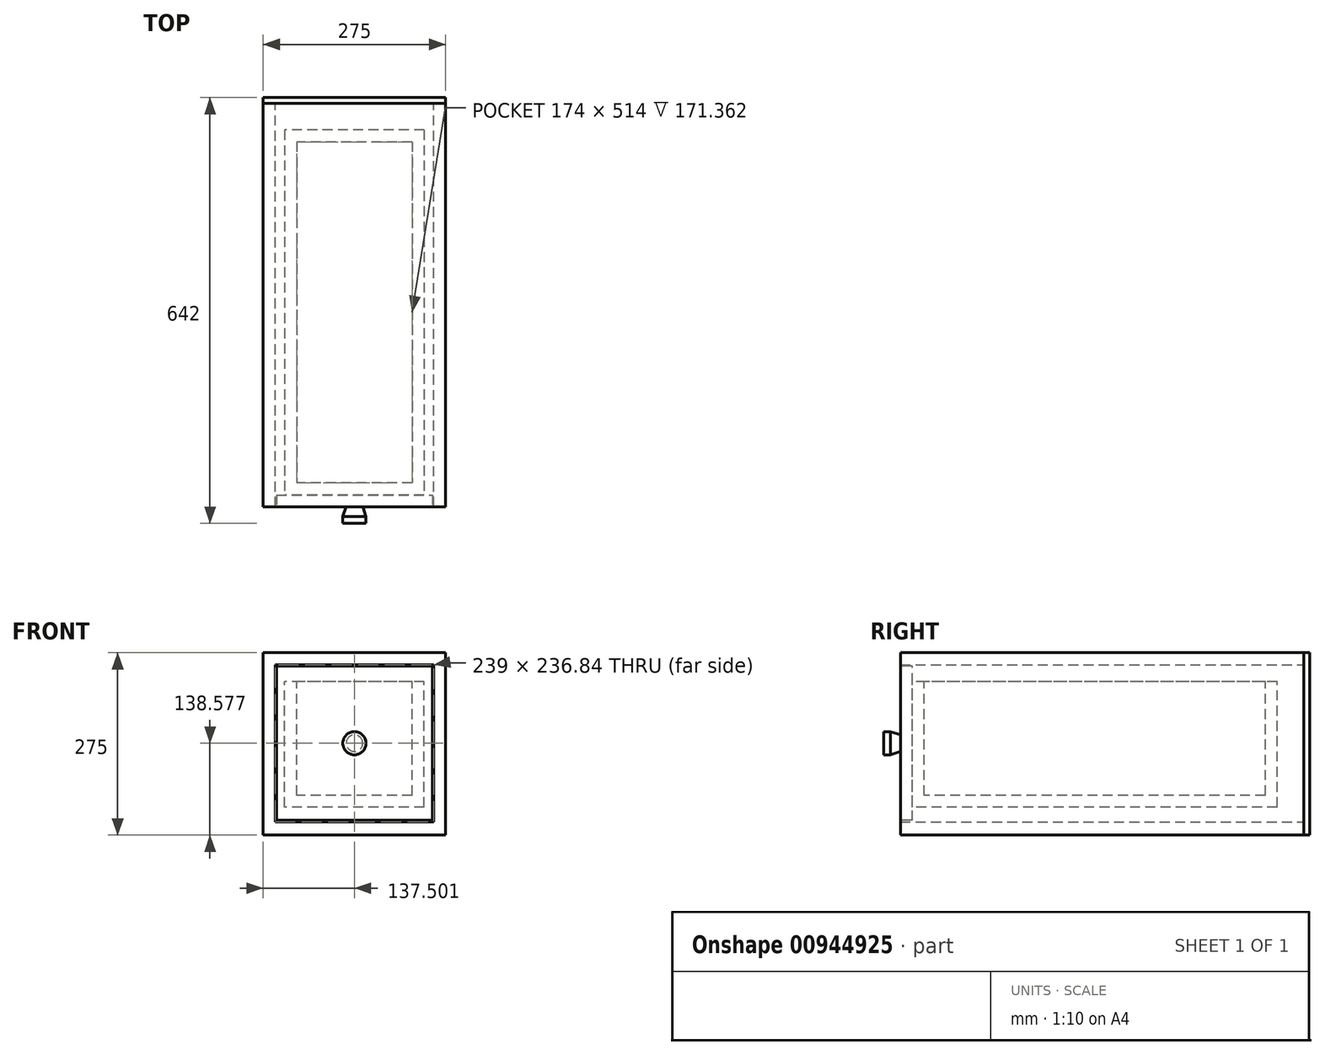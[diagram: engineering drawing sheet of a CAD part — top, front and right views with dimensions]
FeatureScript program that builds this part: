
annotation { "Feature Type Name" : "Feature", "Feature Type Description" : "" }
export const myFeature = defineFeature(function(context is Context, id is Id, definition is map)
    precondition{}
    {
        {
            var Q0;
            Q0=qCreatedBy(makeId("Front.planeOp"),FACE);
            var sketch = newSketch(context, id + "F0", { "sketchPlane" : qUnion([Q0])});
            skLineSegment(sketch, "E0", {"start": v(-326.85, -71.54) * mm, "end": v(-326.85, 203.46) * mm});
            skLineSegment(sketch, "E1.1", {"start": v(-308.85, -51.38) * mm, "end": v(-308.85, 185.46) * mm});
            skLineSegment(sketch, "E2.trimOffspring", {"start": v(-69.85, -51.38) * mm, "end": v(-308.85, -51.38) * mm});
            skLineSegment(sketch, "E3.top", {"start": v(-308.85, 185.46) * mm, "end": v(-69.85, 185.46) * mm});
            skLineSegment(sketch, "E4.trimOffspring", {"start": v(-69.85, 185.46) * mm, "end": v(-69.85, -51.38) * mm});
            skLineSegment(sketch, "E5", {"start": v(-326.85, 203.46) * mm, "end": v(-51.85, 203.46) * mm});
            skLineSegment(sketch, "E6", {"start": v(-51.85, -71.54) * mm, "end": v(-51.85, 203.46) * mm});
            skLineSegment(sketch, "E7", {"start": v(-326.85, -71.54) * mm, "end": v(-51.85, -71.54) * mm});
            skSolve(sketch);
        }
        {
            var Q0;
            Q0=qSketchRegion(id+"F0",true);
            extrude(context, id + "F1", {"entities" : qUnion([Q0]), "depth" : 608 * mm, "offsetDistance" : 25 * mm});
        }
        {
            var Q0;
            Q0=makeQuery(id+"F1.opExtrude","CAP_FACE",FACE,{"disambiguationData":[OSD([sQuery(id+"F0.wireOp",EDGE,"E0"),sQuery(id+"F0.wireOp",EDGE,"1bbb11d5-5f90-4ef2-9ceb-a32cb31813a0"),sQuery(id+"F0.wireOp",EDGE,"E1.1"),sQuery(id+"F0.wireOp",EDGE,"E2.trimOffspring"),sQuery(id+"F0.wireOp",EDGE,"E3.top"),sQuery(id+"F0.wireOp",EDGE,"E4.trimOffspring"),sQuery(id+"F0.wireOp",EDGE,"E5"),sQuery(id+"F0.wireOp",EDGE,"E6")])],"isStart":true});
            var sketch = newSketch(context, id + "F2", { "sketchPlane" : qUnion([Q0])});
            skLineSegment(sketch, "E8.left", {"start": v(51.85, 203.46) * mm, "end": v(51.85, 203.46) * mm});
            skLineSegment(sketch, "E8.right", {"start": v(326.85, 203.46) * mm, "end": v(326.85, 203.46) * mm});
            skLineSegment(sketch, "E9.bottom", {"start": v(51.85, 203.46) * mm, "end": v(326.85, 203.46) * mm});
            skLineSegment(sketch, "E9.top", {"start": v(51.85, -71.54) * mm, "end": v(326.85, -71.54) * mm});
            skLineSegment(sketch, "E9.left", {"start": v(51.85, 203.46) * mm, "end": v(51.85, -71.54) * mm});
            skLineSegment(sketch, "E9.right", {"start": v(326.85, 203.46) * mm, "end": v(326.85, -71.54) * mm});
            skSolve(sketch);
        }
        {
            var Q0;
            Q0=qSketchRegion(id+"F2",true);
            extrude(context, id + "F3", {"entities" : qUnion([Q0]), "depth" : 9 * mm, "offsetDistance" : 25 * mm});
        }
        {
            var Q0;
            Q0=makeQuery(id+"F1.opExtrude","CAP_FACE",FACE,{"disambiguationData":[OSD([sQuery(id+"F0.wireOp",EDGE,"E0"),sQuery(id+"F0.wireOp",EDGE,"1bbb11d5-5f90-4ef2-9ceb-a32cb31813a0"),sQuery(id+"F0.wireOp",EDGE,"E1.1"),sQuery(id+"F0.wireOp",EDGE,"E2.trimOffspring"),sQuery(id+"F0.wireOp",EDGE,"E3.top"),sQuery(id+"F0.wireOp",EDGE,"E4.trimOffspring"),sQuery(id+"F0.wireOp",EDGE,"E5"),sQuery(id+"F0.wireOp",EDGE,"E6")])],"isStart":false});
            var sketch = newSketch(context, id + "F4", { "sketchPlane" : qUnion([Q0])});
            skLineSegment(sketch, "E10.0", {"start": v(-306.85, 183.46) * mm, "end": v(-71.85, 183.46) * mm});
            skLineSegment(sketch, "E10.1", {"start": v(-306.85, -49.38) * mm, "end": v(-306.85, 183.46) * mm});
            skLineSegment(sketch, "E10.2", {"start": v(-71.85, -49.38) * mm, "end": v(-306.85, -49.38) * mm});
            skLineSegment(sketch, "E10.3", {"start": v(-71.85, 183.46) * mm, "end": v(-71.85, -49.38) * mm});
            skSolve(sketch);
        }
        {
            var Q0;
            Q0=qSketchRegion(id+"F4",true);
            extrude(context, id + "F5", {"entities" : qUnion([Q0]), "oppositeDirection" : true, "depth" : 18 * mm, "offsetDistance" : 25 * mm});
        }
        {
            var Q0;
            Q0=makeQuery(id+"F5.opExtrude","CAP_FACE",FACE,{"disambiguationData":[OSD([sQuery(id+"F4.wireOp",EDGE,"E10.0"),sQuery(id+"F4.wireOp",EDGE,"E10.1"),sQuery(id+"F4.wireOp",EDGE,"E10.2"),sQuery(id+"F4.wireOp",EDGE,"E10.3")])],"isStart":false});
            var sketch = newSketch(context, id + "F6", { "sketchPlane" : qUnion([Q0])});
            skLineSegment(sketch, "E11.bottom", {"start": v(84.35, -29.38) * mm, "end": v(294.35, -29.38) * mm});
            skLineSegment(sketch, "E11.top", {"start": v(84.35, 159.98) * mm, "end": v(294.35, 159.98) * mm});
            skLineSegment(sketch, "E11.left", {"start": v(84.35, -29.38) * mm, "end": v(84.35, 159.98) * mm});
            skLineSegment(sketch, "E11.right", {"start": v(294.35, -29.38) * mm, "end": v(294.35, 159.98) * mm});
            skSolve(sketch);
        }
        {
            var Q0;
            Q0=qSketchRegion(id+"F6",true);
            extrude(context, id + "F7", {"entities" : qUnion([Q0]), "depth" : 550 * mm, "offsetDistance" : 25 * mm});
        }
        {
            var Q0;
            Q0=makeQuery(id+"F7.opExtrude","SWEPT_FACE",FACE,{"disambiguationData":[OSD([sQuery(id+"F6.wireOp",EDGE,"E11.top")])]});
            shell(context, id + "F8", {"entities" : qUnion([Q0]), "thickness" : 18 * mm});
        }
        {
            var Q0;
            Q0=makeQuery(id+"F5.opExtrude","CAP_FACE",FACE,{"disambiguationData":[OSD([sQuery(id+"F4.wireOp",EDGE,"E10.0"),sQuery(id+"F4.wireOp",EDGE,"E10.1"),sQuery(id+"F4.wireOp",EDGE,"E10.2"),sQuery(id+"F4.wireOp",EDGE,"E10.3")])],"isStart":true});
            var sketch = newSketch(context, id + "F9", { "sketchPlane" : qUnion([Q0])});
            skLineSegment(sketch, "E12", {"start": v(-71.85, 67.04) * mm, "end": v(-306.85, 67.04) * mm, "construction": true});
            skCircle(sketch, "E13", {"center": v(-189.35, 67.04) * mm, "radius": 17.5 * mm});
            skSolve(sketch);
        }
        {
            var Q0;
            Q0=qSketchRegion(id+"F9",true);
            extrude(context, id + "F10", {"entities" : qUnion([Q0]), "depth" : 25 * mm, "offsetDistance" : 25 * mm});
        }
        {
            var Q0;
            Q0=makeQuery(id+"F10.opExtrude","CAP_EDGE",EDGE,{"disambiguationData":[OSD([sQuery(id+"F9.wireOp",EDGE,"E13")])],"isStart":true});
            chamfer(context, id + "F11", {"entities" : qUnion([Q0]), "chamferType" : ChamferType.TWO_OFFSETS, "width1" : 15 * mm, "oppositeDirection" : false, "width2" : 5 * mm, "tangentPropagation" : true});
        }
    });
